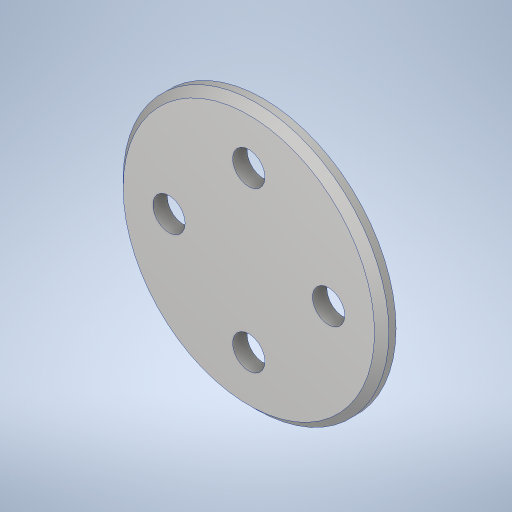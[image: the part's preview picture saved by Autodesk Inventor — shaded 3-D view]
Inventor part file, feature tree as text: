
AUTODESK INVENTOR PART (.ipt)
format: ipt  version: 2023.3 (Build 273359000, 359)  size: 250,880 bytes
history: native  units: in
note: dims shown in document units (in); Inventor stores cm internally (conversion verified against a paired STEP export)
features: sketch x2, extrude x1, chamfer x1, hole x1
ambient origin geometry x8: Origin, YZ Plane, XZ Plane, XY Plane, X Axis, Y Axis, Z Axis, Center Point
bodies: Solid1 (feature_tree)
feature tree (5):
  extrude  "Extrusion1"  Depth=0.0787in TaperAngle=0.0deg
  chamfer  "Chamfer1"  Distance=0.0394in Angle=45.0deg
  hole  "Hole1"  [1 undecoded]
  sketch  "Sketch1"  dims[d0=1.4567in d1=0.0787in d2=0.0in d3=0.0394in d4=0.125in d5=45.0deg]
  sketch  "Sketch2"  dims[d6=0.875in d7=1.5748in d9=360.0deg d11=0.177in d12=0.75in d13=0.332in d14=0.25in d15=0.5635in d16=1.0in d17=0.8108in]
note: 1 required parameter value undecoded (feature->parameter linkage not recoverable at this tier; creation-order binding heuristic only, values carry confidence <= 0.55)
